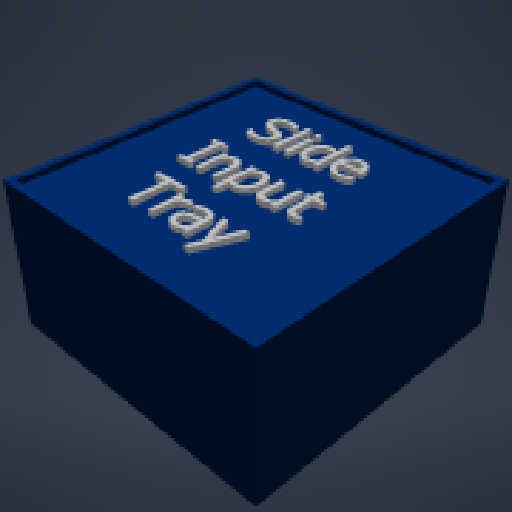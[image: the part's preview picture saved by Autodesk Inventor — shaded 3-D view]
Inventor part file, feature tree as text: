
AUTODESK INVENTOR PART (.ipt)
format: ipt  version: 2025.1 (Build 291241000, 241)  size: 507,392 bytes
history: native  units: mm
features: extrude x3, sketch x2
ambient origin geometry x8: Origin, YZ Plane, XZ Plane, XY Plane, X Axis, Y Axis, Z Axis, Center Point
bodies: Solid1 (feature_tree)
feature tree (5):
  sketch  "Sketch1"  dims[d0=100.0mm d1=100.0mm]
  extrude  "Extrusion1"  Depth=100.0mm
  extrude  "Extrusion2"  Depth=50.0mm TaperAngle=0.0deg
  extrude  "Extrusion3"  Depth=2.0mm TaperAngle=0.0deg
  sketch  "Sketch2"  dims[d3=95.0mm d4=50.0mm d5=0.0mm d6=2.0mm d7=0.0mm d8=2.0mm d9=0.0mm]
